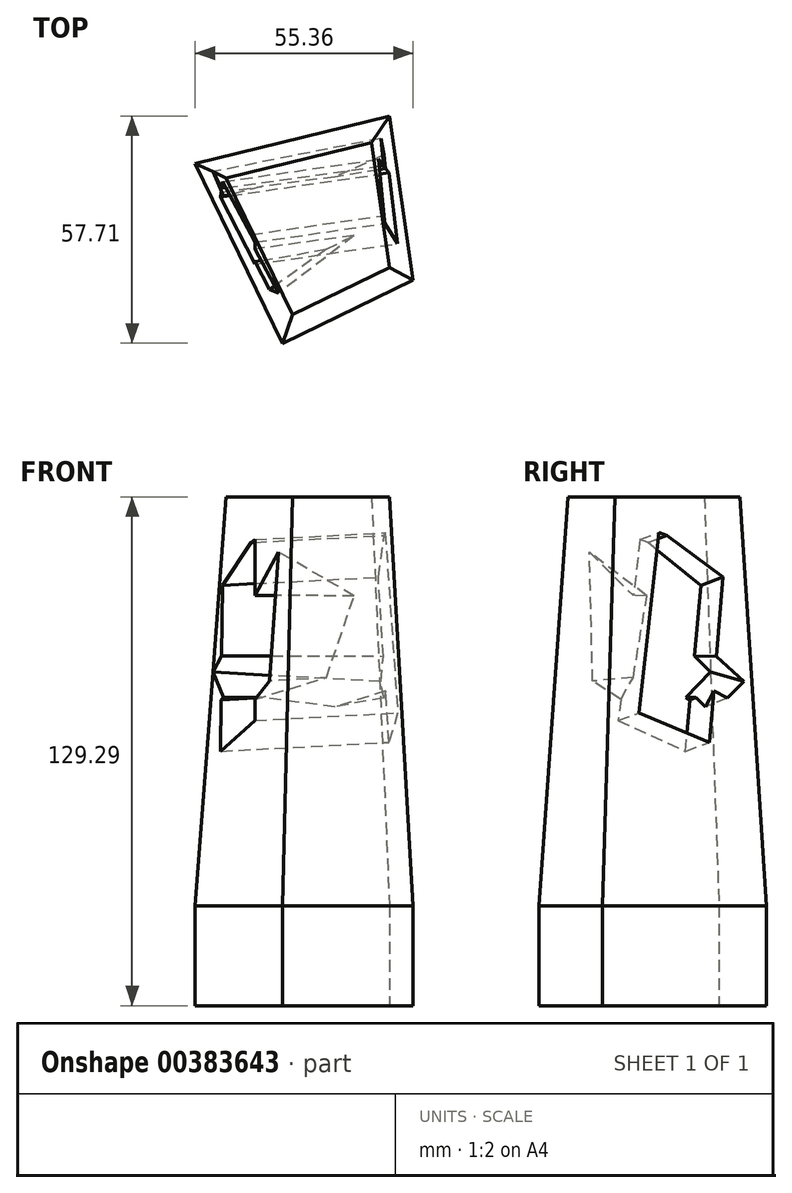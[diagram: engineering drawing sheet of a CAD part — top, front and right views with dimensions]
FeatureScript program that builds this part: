
annotation { "Feature Type Name" : "Feature", "Feature Type Description" : "" }
export const myFeature = defineFeature(function(context is Context, id is Id, definition is map)
    precondition{}
    {
        {
            var Q0;
            Q0=qCreatedBy(makeId("Top.planeOp"),FACE);
            var sketch = newSketch(context, id + "F0", { "sketchPlane" : qUnion([Q0])});
            skLineSegment(sketch, "E0", {"start": v(-48.16, 33.08) * mm, "end": v(-25.96, -12.61) * mm});
            skLineSegment(sketch, "E1", {"start": v(-25.96, -12.61) * mm, "end": v(7.2, 3.5) * mm});
            skLineSegment(sketch, "E2", {"start": v(7.2, 3.5) * mm, "end": v(1.2, 45.1) * mm});
            skLineSegment(sketch, "E3", {"start": v(1.2, 45.1) * mm, "end": v(-48.16, 33.08) * mm});
            skSolve(sketch);
        }
        {
            var Q0;
            Q0=makeQuery(id+"F0.imprint","IMPRINT",FACE,{"disambiguationData":[TD([[makeQuery(id+"F0.imprint","IMPRINT",EDGE,{"derivedFrom":sQuery(id+"F0.wireOp",EDGE,"E0")}),1.0]])]});
            extrude(context, id + "F1", {"entities" : qUnion([Q0]), "depth" : 103.89 * mm, "hasDraft" : true, "draftAngle" : 3 * degree, "draftPullDirection" : true, "hasSecondDirection" : true, "secondDirectionOppositeDirection" : true, "secondDirectionDepth" : 25.4 * mm});
        }
        {
            var Q0;
            Q0=makeQuery(id+"F1.*.split.splitOp","SPLIT",FACE,{"derivedFrom":makeQuery(id+"F1.opExtrude","SWEPT_FACE",FACE,{"disambiguationData":[OSD([sQuery(id+"F0.wireOp",EDGE,"E0")])]})});
            var sketch = newSketch(context, id + "F2", { "sketchPlane" : qUnion([Q0])});
            skLineSegment(sketch, "E4", {"start": v(-48.4, 56.75) * mm, "end": v(-34.03, 43.64) * mm});
            skLineSegment(sketch, "E5", {"start": v(-34.03, 43.64) * mm, "end": v(-15.08, 55.25) * mm});
            skLineSegment(sketch, "E6", {"start": v(-15.08, 55.25) * mm, "end": v(-14.16, 88.1) * mm});
            skLineSegment(sketch, "E7", {"start": v(-14.16, 88.1) * mm, "end": v(-48.4, 56.75) * mm});
            skSolve(sketch);
        }
        {
            var Q0;
            Q0=makeQuery(id+"F2.imprint","IMPRINT",FACE,{"disambiguationData":[TD([[makeQuery(id+"F2.imprint","IMPRINT",EDGE,{"derivedFrom":sQuery(id+"F2.wireOp",EDGE,"E4")}),1.0]])]});
            extrude(context, id + "F3", {"entities" : qUnion([Q0]), "operationType" : NewBodyOperationType.REMOVE, "endBound" : BoundingType.THROUGH_ALL, "oppositeDirection" : true, "depth" : 30.99 * mm, "hasDraft" : true, "draftAngle" : 10 * degree, "draftPullDirection" : true});
        }
        {
            var Q0;
            Q0=makeQuery(id+"F1.*.split.splitOp","SPLIT",FACE,{"derivedFrom":makeQuery(id+"F1.opExtrude","SWEPT_FACE",FACE,{"disambiguationData":[OSD([sQuery(id+"F0.wireOp",EDGE,"E2")])]})});
            var sketch = newSketch(context, id + "F4", { "sketchPlane" : qUnion([Q0])});
            skLineSegment(sketch, "E8", {"start": v(16.92, 94.62) * mm, "end": v(11.74, 48.74) * mm});
            skLineSegment(sketch, "E9", {"start": v(11.74, 48.74) * mm, "end": v(29.94, 41.4) * mm});
            skLineSegment(sketch, "E10", {"start": v(29.94, 41.4) * mm, "end": v(33.4, 83.45) * mm});
            skLineSegment(sketch, "E11", {"start": v(33.4, 83.45) * mm, "end": v(19, 93.96) * mm});
            skLineSegment(sketch, "E12", {"start": v(19, 93.96) * mm, "end": v(16.92, 94.62) * mm});
            skLineSegment(sketch, "E13", {"start": v(19.48, 98.25) * mm, "end": v(33.4, 117.66) * mm});
            skLineSegment(sketch, "E14", {"start": v(26.44, 107.96) * mm, "end": v(26.44, 103.83) * mm});
            skLineSegment(sketch, "E15", {"start": v(26.44, 103.83) * mm, "end": v(27.13, 107.78) * mm});
            skLineSegment(sketch, "E16", {"start": v(27.13, 107.78) * mm, "end": v(26.44, 103.83) * mm, "construction": true});
            skLineSegment(sketch, "E17", {"start": v(27.13, 107.78) * mm, "end": v(26.44, 114.22) * mm, "construction": true});
            skLineSegment(sketch, "E18", {"start": v(26.44, 114.22) * mm, "end": v(25.1, 103.9) * mm, "construction": true});
            skLineSegment(sketch, "E19", {"start": v(25.1, 103.9) * mm, "end": v(25.1, 91.21) * mm, "construction": true});
            skLineSegment(sketch, "E20", {"start": v(25.1, 91.21) * mm, "end": v(19.48, 103.78) * mm, "construction": true});
            skSolve(sketch);
        }
        {
            var Q0;
            Q0=makeQuery(id+"F4.imprint","IMPRINT",FACE,{"disambiguationData":[TD([[makeQuery(id+"F4.imprint","IMPRINT",EDGE,{"derivedFrom":sQuery(id+"F4.wireOp",EDGE,"E8")}),1.0]])]});
            extrude(context, id + "F5", {"entities" : qUnion([Q0]), "operationType" : NewBodyOperationType.REMOVE, "endBound" : BoundingType.UP_TO_NEXT, "oppositeDirection" : true, "depth" : 134.32 * mm});
        }
    });
